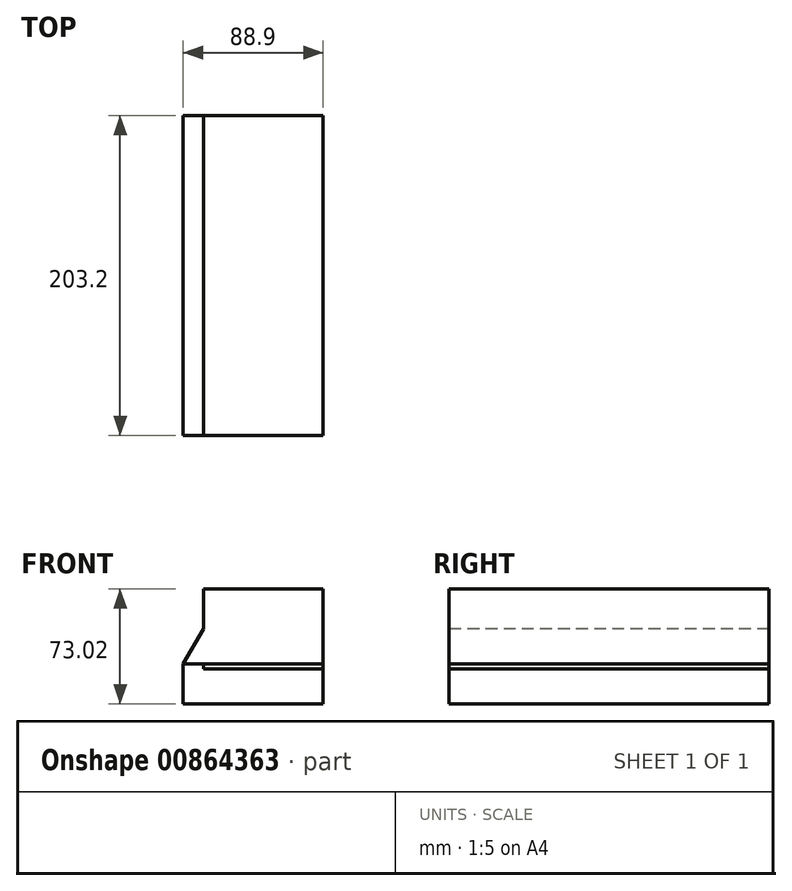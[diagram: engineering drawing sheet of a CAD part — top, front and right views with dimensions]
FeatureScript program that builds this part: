
annotation { "Feature Type Name" : "Feature", "Feature Type Description" : "" }
export const myFeature = defineFeature(function(context is Context, id is Id, definition is map)
    precondition{}
    {
        {
            var Q0;
            Q0=qCreatedBy(makeId("Front.planeOp"),FACE);
            var sketch = newSketch(context, id + "F0", { "sketchPlane" : qUnion([Q0])});
            skLineSegment(sketch, "E0", {"start": v(0, 0) * mm, "end": v(88.9, 0) * mm});
            skLineSegment(sketch, "E1", {"start": v(88.9, 0) * mm, "end": v(88.9, 22.23) * mm});
            skLineSegment(sketch, "E2", {"start": v(88.9, 22.23) * mm, "end": v(12.83, 22.22) * mm});
            skLineSegment(sketch, "E3", {"start": v(12.83, 22.22) * mm, "end": v(0, 0) * mm});
            skSolve(sketch);
        }
        {
            var Q0;
            Q0 = qSketchRegion(id + "F0", true);
            extrude(context, id + "F1", {"entities" : qUnion([Q0]), "endBound" : BoundingType.SYMMETRIC, "oppositeDirection" : true, "depth" : 203.2 * mm, "offsetDistance" : 25.4 * mm});
        }
        {
            var Q0;
            Q0=makeQuery(id+"F1.opExtrude","SWEPT_FACE",FACE,{"disambiguationData":[OSD([sQuery(id+"F0.wireOp",EDGE,"E2")])]});
            cPlane(context, id + "F2", {"entities" : qUnion([Q0]), "cplaneType" : CPlaneType.OFFSET, "offset" : 25.4 * mm, "width" : 152.4 * mm, "height" : 152.4 * mm});
        }
        {
            var Q0;
            Q0=makeQuery(id+"F1.opExtrude","SWEPT_FACE",FACE,{"disambiguationData":[OSD([sQuery(id+"F0.wireOp",EDGE,"E2")])]});
            var sketch = newSketch(context, id + "F3", { "sketchPlane" : qUnion([Q0])});
            skArc(sketch, "E4", {"start": v(34.52, 75.37) * mm, "mid": v(27.73, 69.5) * mm, "end": v(33.6, 62.7) * mm});
            skArc(sketch, "E5", {"start": v(67.62, 62.68) * mm, "mid": v(73.98, 69.03) * mm, "end": v(67.62, 75.38) * mm});
            skLineSegment(sketch, "E6", {"start": v(33.6, 75.36) * mm, "end": v(67.62, 75.38) * mm});
            skLineSegment(sketch, "E7.MirrorCS", {"start": v(33.6, 62.7) * mm, "end": v(67.62, 62.68) * mm});
            skSolve(sketch);
        }
        {
            var Q0;
            {var subQ3=sQuery(id+"F3.wireOp",EDGE,"E5");Q0=makeQuery(id+"F3.imprint","IMPRINT",FACE,{"disambiguationData":[TD([[makeQuery(id+"F3.imprint","IMPRINT",EDGE,{"derivedFrom":subQ3}),1.0]])]});}
            var Q1;
            {var subQ3=sQuery(id+"F3.wireOp",EDGE,"E5");Q1=makeQuery(id+"F3.imprint","IMPRINT",FACE,{"disambiguationData":[TD([[makeQuery(id+"F3.imprint","IMPRINT",EDGE,{"derivedFrom":subQ3}),-1.0]])]});}
            var Q2;
            Q2=makeQuery(id+"F1.opExtrude","SWEPT_FACE",FACE,{"disambiguationData":[OSD([sQuery(id+"F0.wireOp",EDGE,"E2")])]});
            var Q3;
            Q3=makeQuery(id+"F1.opExtrude","SWEPT_FACE",FACE,{"disambiguationData":[OSD([sQuery(id+"F0.wireOp",EDGE,"E0")])]});
            extrude(context, id + "F4", {"entities" : qUnion([Q0, Q1, Q2, Q3]), "oppositeDirection" : true, "depth" : 25.4 * mm, "offsetDistance" : 25.4 * mm});
        }
        {
            var Q0;
            Q0=makeQuery(id+"F1.opExtrude","SWEPT_FACE",FACE,{"disambiguationData":[OSD([sQuery(id+"F0.wireOp",EDGE,"E2")])]});
            var sketch = newSketch(context, id + "F5", { "sketchPlane" : qUnion([Q0])});
            skSolve(sketch);
        }
        {
            var Q0;
            Q0 = qSketchRegion(id + "F5", true);
            var Q1;
            {var subQ0=sQuery(id+"F0.wireOp",EDGE,"E2");Q1=makeQuery(id+"F5.imprint","IMPRINT",FACE,{"disambiguationData":[TD([[makeQuery(id+"F5.imprint","IMPRINT",EDGE,{"derivedFrom":makeQuery(id+"F1.opExtrude","CAP_EDGE",EDGE,{"disambiguationData":[OSD([subQ0])],"isStart":true})}),-1.0]])]});}
            extrude(context, id + "F6", {"entities" : qUnion([Q0, Q1]), "operationType" : NewBodyOperationType.ADD, "depth" : 25.4 * mm, "offsetDistance" : 25.4 * mm});
        }
    });
